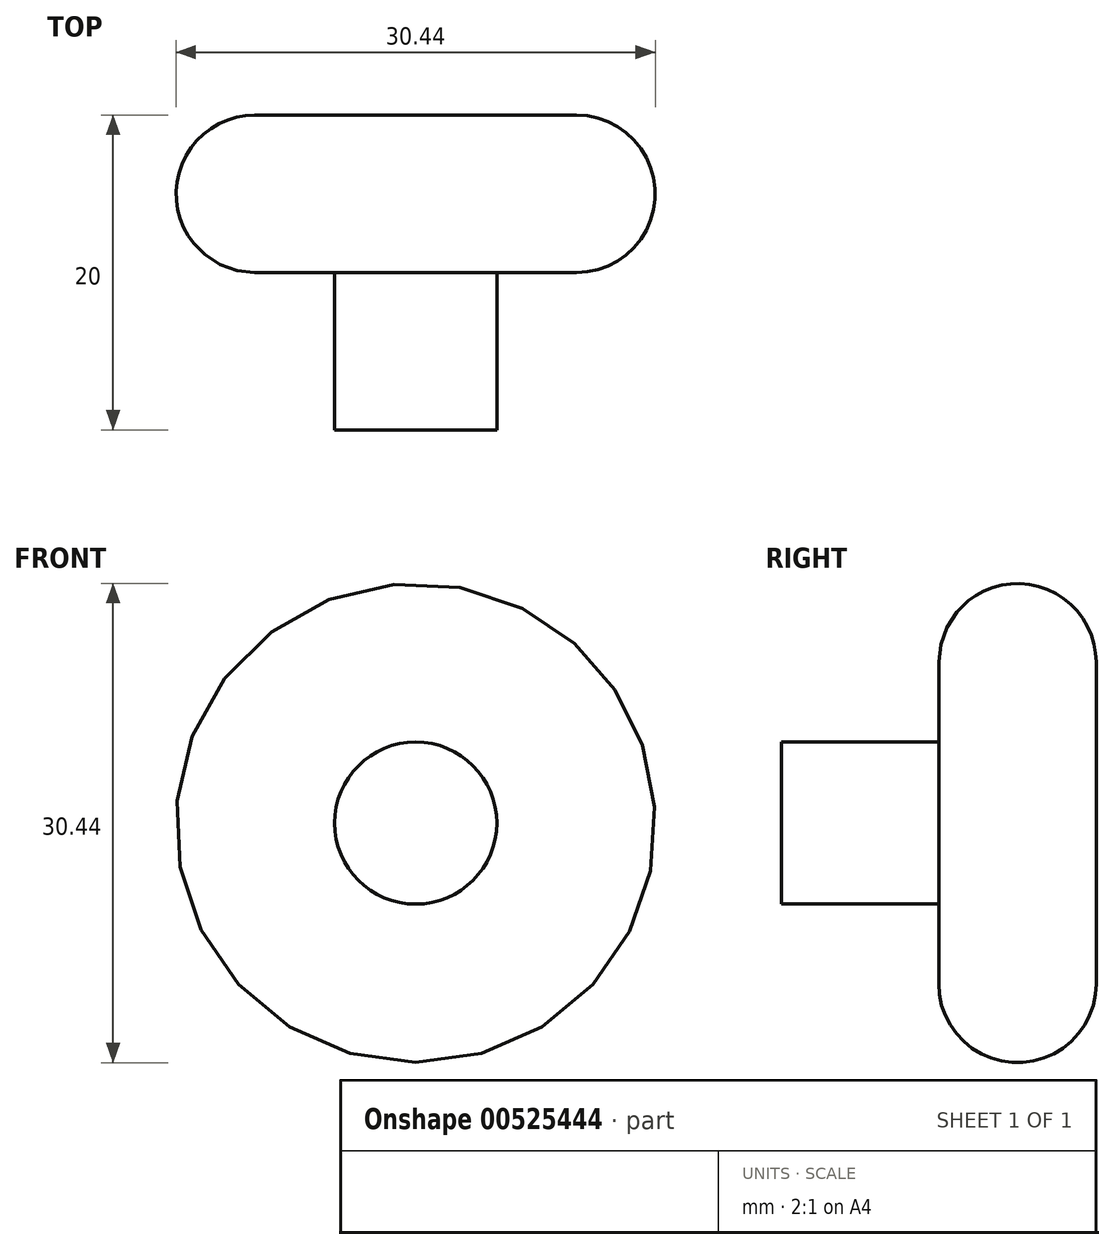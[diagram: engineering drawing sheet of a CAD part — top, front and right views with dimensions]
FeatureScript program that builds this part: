
annotation { "Feature Type Name" : "Feature", "Feature Type Description" : "" }
export const myFeature = defineFeature(function(context is Context, id is Id, definition is map)
    precondition{}
    {
        {
            var Q0;
            Q0=qCreatedBy(makeId("Front.planeOp"),FACE);
            var sketch = newSketch(context, id + "F0", { "sketchPlane" : qUnion([Q0])});
            skCircle(sketch, "E0", {"center": v(0, 0) * mm, "radius": 15.22 * mm});
            skSolve(sketch);
        }
        {
            var Q0;
            Q0=makeQuery(id+"F0.imprint","IMPRINT",FACE,{"disambiguationData":[TD([[makeQuery(id+"F0.imprint","IMPRINT",EDGE,{"derivedFrom":sQuery(id+"F0.wireOp",EDGE,"E0")}),1.0]])]});
            extrude(context, id + "F1", {"entities" : qUnion([Q0]), "depth" : 10 * mm, "offsetDistance" : 25 * mm});
        }
        {
            var Q0;
            Q0=makeQuery(id+"F1.opExtrude","CAP_FACE",FACE,{"disambiguationData":[OSD([sQuery(id+"F0.wireOp",EDGE,"E0")])],"isStart":false});
            var sketch = newSketch(context, id + "F2", { "sketchPlane" : qUnion([Q0])});
            skCircle(sketch, "E1", {"center": v(0, 0) * mm, "radius": 5.15 * mm});
            skSolve(sketch);
        }
        {
            var Q0;
            Q0=makeQuery(id+"F2.imprint","IMPRINT",FACE,{"disambiguationData":[TD([[makeQuery(id+"F2.imprint","IMPRINT",EDGE,{"derivedFrom":sQuery(id+"F2.wireOp",EDGE,"E1")}),1.0]])]});
            extrude(context, id + "F3", {"entities" : qUnion([Q0]), "operationType" : NewBodyOperationType.ADD, "depth" : 10 * mm, "offsetDistance" : 25 * mm});
        }
        {
            var Q0;
            Q0=makeQuery(id+"F1.opExtrude","SWEPT_FACE",FACE,{"disambiguationData":[OSD([sQuery(id+"F0.wireOp",EDGE,"E0")])]});
            fillet(context, id + "F4", {"entities" : qUnion([Q0]), "radius" : 5 * mm, "tangentPropagation" : true, "allowEdgeOverflow" : false});
        }
    });
